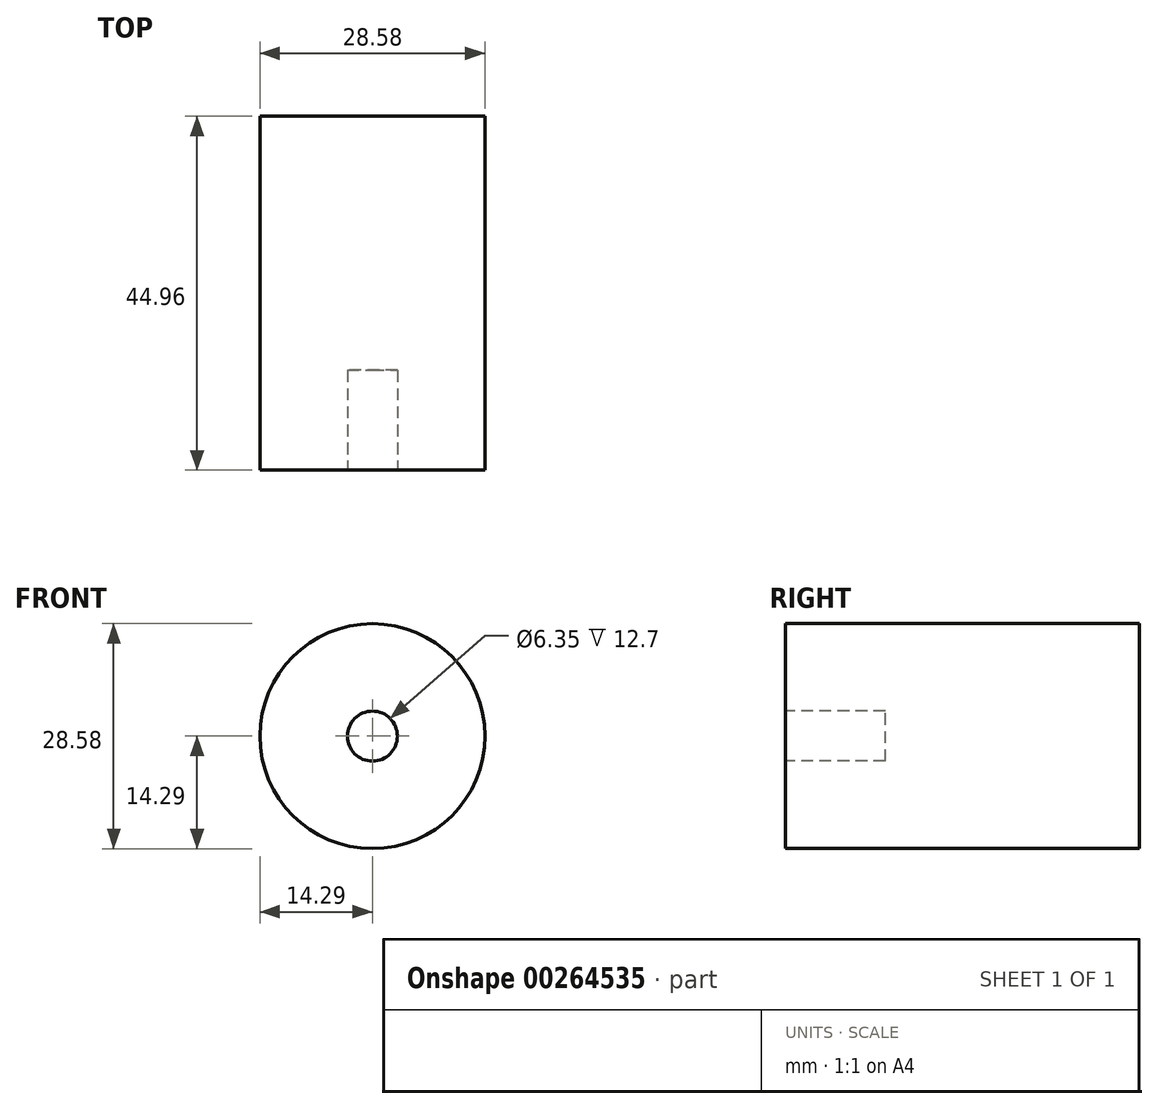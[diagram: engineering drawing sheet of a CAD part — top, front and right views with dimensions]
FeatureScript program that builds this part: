
annotation { "Feature Type Name" : "Feature", "Feature Type Description" : "" }
export const myFeature = defineFeature(function(context is Context, id is Id, definition is map)
    precondition{}
    {
        {
            var Q0;
            Q0=qCreatedBy(makeId("Front.planeOp"),FACE);
            var sketch = newSketch(context, id + "F3", { "sketchPlane" : qUnion([Q0])});
            skCircle(sketch, "E0", {"center": v(0, 0) * mm, "radius": 14.29 * mm});
            skSolve(sketch);
        }
        {
            var Q0;
            Q0 = qSketchRegion(id + "F3", true);
            extrude(context, id + "F0", {"entities" : qUnion([Q0]), "depth" : 38.1 * mm + 6.86 * mm, "symmetric" : true});
        }
        {
            var Q0;
            Q0=makeQuery(id+"F0.opExtrude","CAP_FACE",FACE,{"disambiguationData":[OSD([sQuery(id+"F3.wireOp",EDGE,"E0")])],"isStart":false});
            var sketch = newSketch(context, id + "F1", { "sketchPlane" : qUnion([Q0])});
            skCircle(sketch, "E1", {"center": v(0, 0) * mm, "radius": 3.18 * mm});
            skSolve(sketch);
        }
        {
            var Q0;
            Q0 = qSketchRegion(id + "F1", true);
            extrude(context, id + "F2", {"entities" : qUnion([Q0]), "operationType" : NewBodyOperationType.REMOVE, "oppositeDirection" : true, "depth" : 12.7 * mm});
        }
    });
